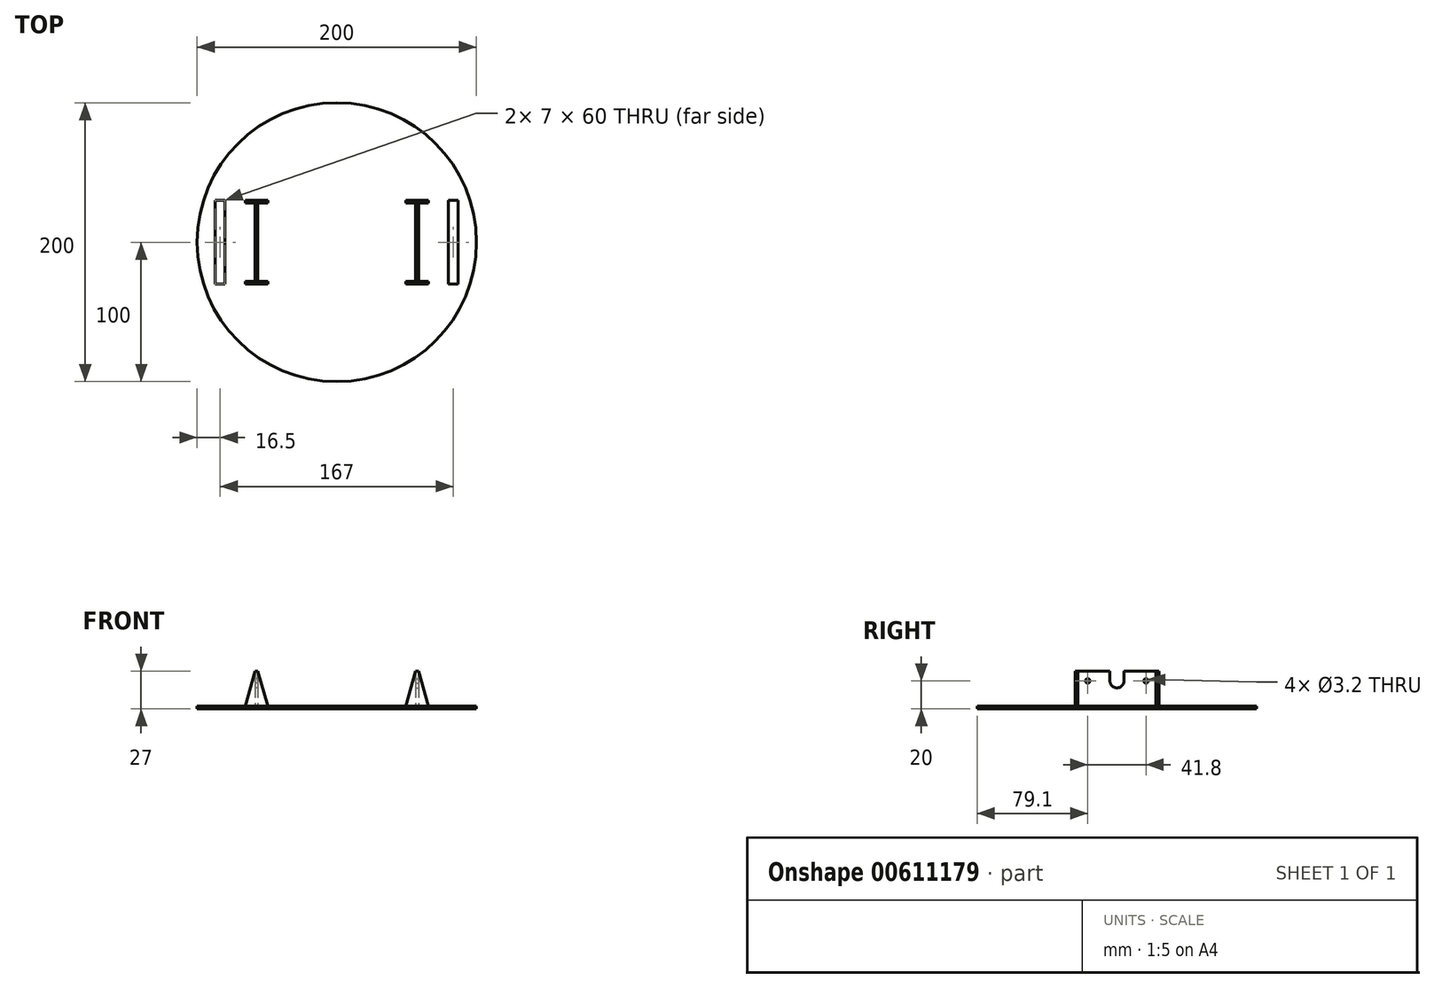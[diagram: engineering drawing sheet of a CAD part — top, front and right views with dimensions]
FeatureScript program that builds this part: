
annotation { "Feature Type Name" : "Feature", "Feature Type Description" : "" }
export const myFeature = defineFeature(function(context is Context, id is Id, definition is map)
    precondition{}
    {
        {
            var Q0;
            Q0=qCreatedBy(makeId("Top.planeOp"),FACE);
            var sketch = newSketch(context, id + "F0", { "sketchPlane" : qUnion([Q0])});
            skCircle(sketch, "E0", {"center": v(0, 0) * mm, "radius": 100 * mm});
            skLineSegment(sketch, "E1.bottom", {"start": v(-80, 30) * mm, "end": v(-87, 30) * mm});
            skLineSegment(sketch, "E1.top", {"start": v(-80, -30) * mm, "end": v(-87, -30) * mm});
            skLineSegment(sketch, "E1.left", {"start": v(-80, 30) * mm, "end": v(-80, -30) * mm});
            skLineSegment(sketch, "E1.right", {"start": v(-87, 30) * mm, "end": v(-87, -30) * mm});
            skPoint(sketch, "E1.middle", {"position": v(-83.5, 0) * mm});
            skLineSegment(sketch, "E2.MirrorCS", {"start": v(80, 30) * mm, "end": v(87, 30) * mm});
            skLineSegment(sketch, "E3.MirrorCS", {"start": v(80, 30) * mm, "end": v(80, -30) * mm});
            skLineSegment(sketch, "E4.MirrorCS", {"start": v(80, -30) * mm, "end": v(87, -30) * mm});
            skLineSegment(sketch, "E5.MirrorCS", {"start": v(87, 30) * mm, "end": v(87, -30) * mm});
            skPoint(sketch, "E6.MirrorP", {"position": v(83.5, 0) * mm});
            skSolve(sketch);
        }
        {
            var Q0;
            {var subQ0=sQuery(id+"F0.wireOp",EDGE,"K0GAp1Y4-Ixp0-aC1l-omNU-r5FszGDL7PR0.top");var subQ1=sQuery(id+"F0.wireOp",EDGE,"HqlQ3rIF-Y2ew-o2BC-WH6p-pxuWtE5EoVCb.left");var subQ2=makeQuery(id+"F0.imprint","INTERSECT",VERTEX,{"derivedFrom":[subQ1,subQ0]});Q0=makeQuery(id+"F0.imprint","IMPRINT",FACE,{"disambiguationData":[TD([[makeQuery(id+"F0.imprint","IMPRINT",EDGE,{"disambiguationData":[TD([[subQ2,-1.0]])],"derivedFrom":subQ1}),-1.0]])]});}
            var Q1;
            {var subQ5=sQuery(id+"F0.wireOp",EDGE,"K0GAp1Y4-Ixp0-aC1l-omNU-r5FszGDL7PR0.right");Q1=makeQuery(id+"F0.imprint","IMPRINT",FACE,{"disambiguationData":[TD([[makeQuery(id+"F0.imprint","IMPRINT",EDGE,{"derivedFrom":subQ5}),1.0]])]});}
            var Q2;
            {var subQ5=sQuery(id+"F0.wireOp",EDGE,"K0GAp1Y4-Ixp0-aC1l-omNU-r5FszGDL7PR0.left");Q2=makeQuery(id+"F0.imprint","IMPRINT",FACE,{"disambiguationData":[TD([[makeQuery(id+"F0.imprint","IMPRINT",EDGE,{"derivedFrom":subQ5}),-1.0]])]});}
            var Q3;
            {var subQ0=sQuery(id+"F0.wireOp",EDGE,"K0GAp1Y4-Ixp0-aC1l-omNU-r5FszGDL7PR0.bottom");var subQ1=sQuery(id+"F0.wireOp",EDGE,"HqlQ3rIF-Y2ew-o2BC-WH6p-pxuWtE5EoVCb.left");var subQ2=makeQuery(id+"F0.imprint","INTERSECT",VERTEX,{"derivedFrom":[subQ1,subQ0]});Q3=makeQuery(id+"F0.imprint","IMPRINT",FACE,{"disambiguationData":[TD([[makeQuery(id+"F0.imprint","IMPRINT",EDGE,{"disambiguationData":[TD([[subQ2,-1.0]])],"derivedFrom":subQ1}),-1.0]])]});}
            var Q4;
            Q4=makeQuery(id+"F0.imprint","IMPRINT",FACE,{"disambiguationData":[TD([[makeQuery(id+"F0.imprint","IMPRINT",EDGE,{"derivedFrom":sQuery(id+"F0.wireOp",EDGE,"E0")}),1.0]])]});
            var Q5;
            {var subQ5=sQuery(id+"F0.wireOp",EDGE,"2bd450b3-5e51-421b-8461-b64049ee1ff72.MirrorCS");Q5=makeQuery(id+"F0.imprint","IMPRINT",FACE,{"disambiguationData":[TD([[makeQuery(id+"F0.imprint","IMPRINT",EDGE,{"derivedFrom":subQ5}),-1.0]])]});}
            var Q6;
            {var subQ0=sQuery(id+"F0.wireOp",EDGE,"2bd450b3-5e51-421b-8461-b64049ee1ff74.MirrorCS");var subQ1=sQuery(id+"F0.wireOp",EDGE,"HqlQ3rIF-Y2ew-o2BC-WH6p-pxuWtE5EoVCb.left");var subQ2=makeQuery(id+"F0.imprint","INTERSECT",VERTEX,{"derivedFrom":[subQ1,subQ0]});Q6=makeQuery(id+"F0.imprint","IMPRINT",FACE,{"disambiguationData":[TD([[makeQuery(id+"F0.imprint","IMPRINT",EDGE,{"disambiguationData":[TD([[subQ2,1.0]])],"derivedFrom":subQ1}),-1.0]])]});}
            var Q7;
            {var subQ5=sQuery(id+"F0.wireOp",EDGE,"2bd450b3-5e51-421b-8461-b64049ee1ff70.MirrorCS");Q7=makeQuery(id+"F0.imprint","IMPRINT",FACE,{"disambiguationData":[TD([[makeQuery(id+"F0.imprint","IMPRINT",EDGE,{"derivedFrom":subQ5}),1.0]])]});}
            extrude(context, id + "F1", {"entities" : qUnion([Q0, Q1, Q2, Q3, Q4, Q5, Q6, Q7]), "depth" : 2 * mm, "offsetDistance" : 25.4 * mm});
        }
        {
            var Q0;
            Q0=makeQuery(id+"F1.opExtrude","CAP_FACE",FACE,{"disambiguationData":[OSD([sQuery(id+"F0.wireOp",EDGE,"E0"),sQuery(id+"F0.wireOp",EDGE,"E1.bottom"),sQuery(id+"F0.wireOp",EDGE,"E1.top"),sQuery(id+"F0.wireOp",EDGE,"E1.left"),sQuery(id+"F0.wireOp",EDGE,"E1.right"),sQuery(id+"F0.wireOp",EDGE,"E2.MirrorCS"),sQuery(id+"F0.wireOp",EDGE,"E3.MirrorCS"),sQuery(id+"F0.wireOp",EDGE,"E4.MirrorCS"),sQuery(id+"F0.wireOp",EDGE,"E5.MirrorCS")])],"isStart":false});
            var sketch = newSketch(context, id + "F2", { "sketchPlane" : qUnion([Q0])});
            skLineSegment(sketch, "E7.bottom", {"start": v(-56.5, 30) * mm, "end": v(-58.5, 30) * mm});
            skLineSegment(sketch, "E7.left", {"start": v(-56.5, 30) * mm, "end": v(-56.5, -30) * mm});
            skLineSegment(sketch, "E7.right", {"start": v(-58.5, 30) * mm, "end": v(-58.5, -30) * mm});
            skPoint(sketch, "E7.middle", {"position": v(-57.5, 0) * mm});
            skLineSegment(sketch, "E8.bottom", {"start": v(-65.5, 28) * mm, "end": v(-49.5, 28) * mm});
            skLineSegment(sketch, "E8.top", {"start": v(-65.5, 30) * mm, "end": v(-49.5, 30) * mm});
            skLineSegment(sketch, "E8.left", {"start": v(-65.5, 28) * mm, "end": v(-65.5, 30) * mm});
            skLineSegment(sketch, "E8.right", {"start": v(-49.5, 28) * mm, "end": v(-49.5, 30) * mm});
            skLineSegment(sketch, "E9.MirrorCS", {"start": v(-56.5, -30) * mm, "end": v(-58.5, -30) * mm});
            skLineSegment(sketch, "E10.MirrorCS", {"start": v(-65.5, -28) * mm, "end": v(-65.5, -30) * mm});
            skLineSegment(sketch, "E11.MirrorCS", {"start": v(-49.5, -28) * mm, "end": v(-49.5, -30) * mm});
            skLineSegment(sketch, "E12.MirrorCS", {"start": v(-65.5, -28) * mm, "end": v(-49.5, -28) * mm});
            skLineSegment(sketch, "E13.MirrorCS", {"start": v(-65.5, -30) * mm, "end": v(-49.5, -30) * mm});
            skSolve(sketch);
        }
        {
            var Q0;
            {var subQ5=sQuery(id+"F2.wireOp",EDGE,"E8.left");Q0=makeQuery(id+"F2.imprint","IMPRINT",FACE,{"disambiguationData":[TD([[makeQuery(id+"F2.imprint","IMPRINT",EDGE,{"derivedFrom":subQ5}),-1.0]])]});}
            var Q1;
            {var subQ0=sQuery(id+"F2.wireOp",EDGE,"E8.top");var subQ1=sQuery(id+"F2.wireOp",EDGE,"E7.left");var subQ2=makeQuery(id+"F2.imprint","INTERSECT",VERTEX,{"derivedFrom":[subQ1,subQ0]});Q1=makeQuery(id+"F2.imprint","IMPRINT",FACE,{"disambiguationData":[TD([[makeQuery(id+"F2.imprint","IMPRINT",EDGE,{"disambiguationData":[TD([[subQ2,-1.0]])],"derivedFrom":subQ1}),-1.0]])]});}
            var Q2;
            {var subQ5=sQuery(id+"F2.wireOp",EDGE,"E8.right");Q2=makeQuery(id+"F2.imprint","IMPRINT",FACE,{"disambiguationData":[TD([[makeQuery(id+"F2.imprint","IMPRINT",EDGE,{"derivedFrom":subQ5}),1.0]])]});}
            var Q3;
            {var subQ0=sQuery(id+"F2.wireOp",EDGE,"E8.bottom");var subQ1=sQuery(id+"F2.wireOp",EDGE,"E7.left");var subQ2=makeQuery(id+"F2.imprint","INTERSECT",VERTEX,{"derivedFrom":[subQ1,subQ0]});Q3=makeQuery(id+"F2.imprint","IMPRINT",FACE,{"disambiguationData":[TD([[makeQuery(id+"F2.imprint","IMPRINT",EDGE,{"disambiguationData":[TD([[subQ2,-1.0]])],"derivedFrom":subQ1}),-1.0]])]});}
            var Q4;
            {var subQ0=sQuery(id+"F2.wireOp",EDGE,"E13.MirrorCS");var subQ1=sQuery(id+"F2.wireOp",EDGE,"E7.left");var subQ2=makeQuery(id+"F2.imprint","INTERSECT",VERTEX,{"derivedFrom":[subQ1,subQ0]});Q4=makeQuery(id+"F2.imprint","IMPRINT",FACE,{"disambiguationData":[TD([[makeQuery(id+"F2.imprint","IMPRINT",EDGE,{"disambiguationData":[TD([[subQ2,1.0]])],"derivedFrom":subQ1}),-1.0]])]});}
            var Q5;
            {var subQ5=sQuery(id+"F2.wireOp",EDGE,"E10.MirrorCS");Q5=makeQuery(id+"F2.imprint","IMPRINT",FACE,{"disambiguationData":[TD([[makeQuery(id+"F2.imprint","IMPRINT",EDGE,{"derivedFrom":subQ5}),1.0]])]});}
            var Q6;
            {var subQ5=sQuery(id+"F2.wireOp",EDGE,"E11.MirrorCS");Q6=makeQuery(id+"F2.imprint","IMPRINT",FACE,{"disambiguationData":[TD([[makeQuery(id+"F2.imprint","IMPRINT",EDGE,{"derivedFrom":subQ5}),-1.0]])]});}
            extrude(context, id + "F3", {"entities" : qUnion([Q0, Q1, Q2, Q3, Q4, Q5, Q6]), "depth" : (23 + 2) * mm, "offsetDistance" : 25 * mm});
        }
        {
            var Q0;
            Q0=makeQuery(id+"F3.opExtrude","CAP_EDGE",EDGE,{"disambiguationData":[OSD([sQuery(id+"F2.wireOp",EDGE,"E8.left")])],"isStart":false});
            var Q1;
            Q1=makeQuery(id+"F3.opExtrude","CAP_EDGE",EDGE,{"disambiguationData":[OSD([sQuery(id+"F2.wireOp",EDGE,"E8.right")])],"isStart":false});
            var Q2;
            Q2=makeQuery(id+"F3.opExtrude","CAP_EDGE",EDGE,{"disambiguationData":[OSD([sQuery(id+"F2.wireOp",EDGE,"E10.MirrorCS")])],"isStart":false});
            var Q3;
            Q3=makeQuery(id+"F3.opExtrude","CAP_EDGE",EDGE,{"disambiguationData":[OSD([sQuery(id+"F2.wireOp",EDGE,"E11.MirrorCS")])],"isStart":false});
            chamfer(context, id + "F4", {"entities" : qUnion([Q0, Q1, Q2, Q3]), "chamferType" : ChamferType.TWO_OFFSETS, "width1" : 25 * mm, "oppositeDirection" : false, "width2" : 7 * mm, "tangentPropagation" : true});
        }
        {
            var Q0;
            Q0=makeQuery(id+"F3.opExtrude","SWEPT_FACE",FACE,{"disambiguationData":[OSD([sQuery(id+"F2.wireOp",EDGE,"E7.right")])]});
            var sketch = newSketch(context, id + "F5", { "sketchPlane" : qUnion([Q0])});
            skCircle(sketch, "E14", {"center": v(-20.9, 20) * mm, "radius": 1.6 * mm});
            skCircle(sketch, "E15.MirrorC", {"center": v(20.9, 20) * mm, "radius": 1.6 * mm});
            skCircle(sketch, "E16", {"center": v(0, 20) * mm, "radius": 5 * mm});
            skLineSegment(sketch, "E17", {"start": v(-20.9, 20) * mm, "end": v(20.9, 20) * mm, "construction": true});
            skLineSegment(sketch, "E18", {"start": v(-5, 20) * mm, "end": v(-5, 27) * mm});
            skLineSegment(sketch, "E19", {"start": v(5, 20) * mm, "end": v(5, 27) * mm});
            skSolve(sketch);
        }
        {
            var Q0;
            Q0 = qSketchRegion(id + "F5", true);
            var Q1;
            {var subQ0=sQuery(id+"F5.wireOp",EDGE,"E18");Q1=makeQuery(id+"F5.imprint","IMPRINT",FACE,{"disambiguationData":[TD([[makeQuery(id+"F5.imprint","IMPRINT",EDGE,{"derivedFrom":subQ0}),-1.0]])]});}
            extrude(context, id + "F6", {"entities" : qUnion([Q0, Q1]), "operationType" : NewBodyOperationType.REMOVE, "oppositeDirection" : true, "depth" : 2 * mm, "offsetDistance" : 25 * mm});
        }
        {
            var Q0;
            Q0=makeQuery(id+"F6.boolean.opBoolean","COPY",EDGE,{"derivedFrom":makeQuery(id+"F6.opExtrude","SWEPT_EDGE",EDGE,{"disambiguationData":[OSD([sQuery(id+"F2.wireOp",EDGE,"E7.right"),sQuery(id+"F5.wireOp",EDGE,"E18")])]})});
            var Q1;
            Q1=makeQuery(id+"F6.boolean.opBoolean","COPY",EDGE,{"derivedFrom":makeQuery(id+"F6.opExtrude","SWEPT_EDGE",EDGE,{"disambiguationData":[OSD([sQuery(id+"F2.wireOp",EDGE,"E7.right"),sQuery(id+"F5.wireOp",EDGE,"E19")])]})});
            fillet(context, id + "F7", {"entities" : qUnion([Q0, Q1]), "radius" : 1 * mm, "tangentPropagation" : true, "allowEdgeOverflow" : false});
        }
        {
            var Q0;
            Q0=makeQuery(id+"F3.opExtrude","SWEPT_BODY",BODY,{"disambiguationData":[OSD([sQuery(id+"F2.wireOp",EDGE,"E7.left"),sQuery(id+"F2.wireOp",EDGE,"E7.right"),sQuery(id+"F2.wireOp",EDGE,"E8.bottom"),sQuery(id+"F2.wireOp",EDGE,"E8.top"),sQuery(id+"F2.wireOp",EDGE,"E8.left"),sQuery(id+"F2.wireOp",EDGE,"E8.right"),sQuery(id+"F2.wireOp",EDGE,"E10.MirrorCS"),sQuery(id+"F2.wireOp",EDGE,"E11.MirrorCS"),sQuery(id+"F2.wireOp",EDGE,"E12.MirrorCS"),sQuery(id+"F2.wireOp",EDGE,"E13.MirrorCS")])]});
            var Q1;
            Q1=makeQuery(id+"F1.opExtrude","CAP_EDGE",EDGE,{"disambiguationData":[OSD([sQuery(id+"F0.wireOp",EDGE,"E0")])],"isStart":false});
            circularPattern(context, id + "F8", {"entities" : qUnion([Q0]), "axis" : qUnion([Q1]), "angle" : 360 * degree, "instanceCount" : 2, "equalSpace" : true});
        }
    });
